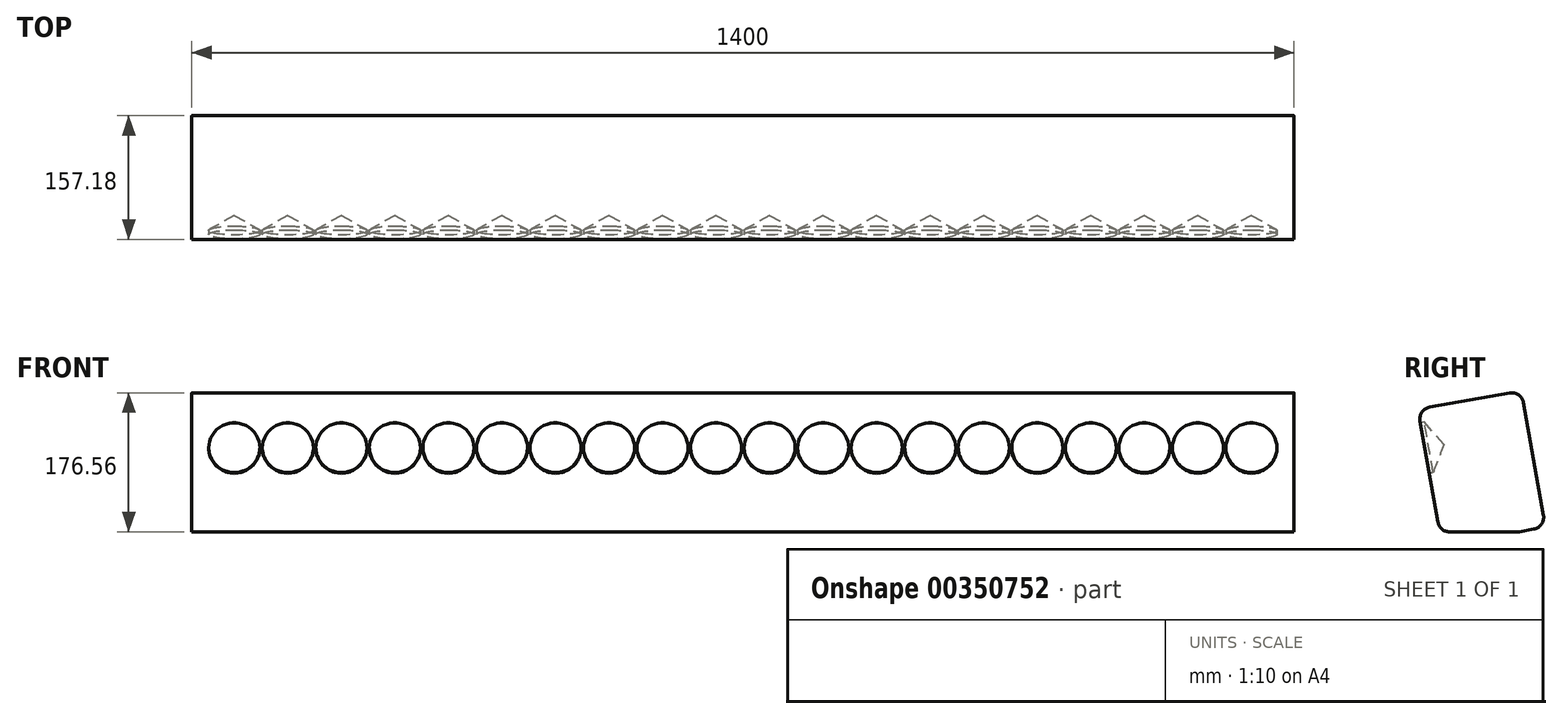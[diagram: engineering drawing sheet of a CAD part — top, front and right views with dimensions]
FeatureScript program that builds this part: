
annotation { "Feature Type Name" : "Feature", "Feature Type Description" : "" }
export const myFeature = defineFeature(function(context is Context, id is Id, definition is map)
    precondition{}
    {
        {
            var Q0;
            Q0=qCreatedBy(makeId("Right.planeOp"),FACE);
            var sketch = newSketch(context, id + "F0", { "sketchPlane" : qUnion([Q0])});
            skLineSegment(sketch, "E0", {"start": v(0, 0) * mm, "end": v(100, 0) * mm});
            skLineSegment(sketch, "E1", {"start": v(100, 0) * mm, "end": v(134.47, 6.08) * mm});
            skLineSegment(sketch, "E2", {"start": v(134.47, 6.08) * mm, "end": v(103.99, 178.94) * mm});
            skLineSegment(sketch, "E3", {"start": v(103.99, 178.94) * mm, "end": v(-27.46, 155.76) * mm});
            skLineSegment(sketch, "E4", {"start": v(-27.46, 155.76) * mm, "end": v(0, 0) * mm});
            skLineSegment(sketch, "E5", {"start": v(0, 0) * mm, "end": v(-507.71, 0) * mm, "construction": true});
            skLineSegment(sketch, "E6", {"start": v(-507.71, 0) * mm, "end": v(-15.3, 86.82) * mm, "construction": true});
            skSolve(sketch);
        }
        {
            var Q0;
            Q0=makeQuery(id+"F0.imprint","IMPRINT",FACE,{"disambiguationData":[TD([[makeQuery(id+"F0.imprint","IMPRINT",EDGE,{"derivedFrom":sQuery(id+"F0.wireOp",EDGE,"E0")}),1.0]])]});
            extrude(context, id + "F1", {"entities" : qUnion([Q0]), "endBound" : BoundingType.SYMMETRIC, "depth" : 1400 * mm});
        }
        {
            var Q0;
            Q0=makeQuery(id+"F1.opExtrude","SWEPT_EDGE",EDGE,{"disambiguationData":[OSD([sQuery(id+"F0.wireOp",EDGE,"E0"),sQuery(id+"F0.wireOp",EDGE,"E1")])]});
            var Q1;
            Q1=makeQuery(id+"F1.opExtrude","SWEPT_EDGE",EDGE,{"disambiguationData":[OSD([sQuery(id+"F0.wireOp",EDGE,"E1"),sQuery(id+"F0.wireOp",EDGE,"E2")])]});
            var Q2;
            Q2=makeQuery(id+"F1.opExtrude","SWEPT_EDGE",EDGE,{"disambiguationData":[OSD([sQuery(id+"F0.wireOp",EDGE,"E2"),sQuery(id+"F0.wireOp",EDGE,"E3")])]});
            var Q3;
            Q3=makeQuery(id+"F1.opExtrude","SWEPT_EDGE",EDGE,{"disambiguationData":[OSD([sQuery(id+"F0.wireOp",EDGE,"E3"),sQuery(id+"F0.wireOp",EDGE,"E4")])]});
            var Q4;
            Q4=makeQuery(id+"F1.opExtrude","SWEPT_EDGE",EDGE,{"disambiguationData":[OSD([sQuery(id+"F0.wireOp",EDGE,"E0"),sQuery(id+"F0.wireOp",EDGE,"E4")])]});
            fillet(context, id + "F2", {"entities" : qUnion([Q0, Q1, Q2, Q3, Q4]), "radius" : 15 * mm, "tangentPropagation" : true, "allowEdgeOverflow" : false});
        }
        {
            var Q0;
            Q0=makeQuery(id+"F1.opExtrude","SWEPT_FACE",FACE,{"disambiguationData":[OSD([sQuery(id+"F0.wireOp",EDGE,"E4")])]});
            var sketch = newSketch(context, id + "F3", { "sketchPlane" : qUnion([Q0])});
            skPoint(sketch, "E7", {"position": v(-34, 108.16) * mm});
            skPoint(sketch, "E8", {"position": v(34, 108.16) * mm});
            skLineSegment(sketch, "E9", {"start": v(-34, 108.16) * mm, "end": v(34, 108.16) * mm, "construction": true});
            skLineSegment(sketch, "E10", {"start": v(0, 0) * mm, "end": v(0, 108.16) * mm, "construction": true});
            skPoint(sketch, "E10.endSnap0", {"position": v(0, 12.59) * mm});
            skPoint(sketch, "E11.1.0.0", {"position": v(102, 108.16) * mm});
            skPoint(sketch, "E11.2.0.0", {"position": v(170, 108.16) * mm});
            skPoint(sketch, "E11.3.0.0", {"position": v(238, 108.16) * mm});
            skPoint(sketch, "E11.4.0.0", {"position": v(306, 108.16) * mm});
            skPoint(sketch, "E11.5.0.0", {"position": v(374, 108.16) * mm});
            skPoint(sketch, "E11.6.0.0", {"position": v(442, 108.16) * mm});
            skPoint(sketch, "E11.7.0.0", {"position": v(510, 108.16) * mm});
            skPoint(sketch, "E11.8.0.0", {"position": v(578, 108.16) * mm});
            skPoint(sketch, "E11.9.0.0", {"position": v(646, 108.16) * mm});
            skLineSegment(sketch, "E11.direction1", {"start": v(34, 108.16) * mm, "end": v(102, 108.16) * mm, "construction": true});
            skPoint(sketch, "E12.1.0.0", {"position": v(-102, 108.16) * mm});
            skPoint(sketch, "E12.2.0.0", {"position": v(-170, 108.16) * mm});
            skPoint(sketch, "E12.3.0.0", {"position": v(-238, 108.16) * mm});
            skPoint(sketch, "E12.4.0.0", {"position": v(-306, 108.16) * mm});
            skPoint(sketch, "E12.5.0.0", {"position": v(-374, 108.16) * mm});
            skPoint(sketch, "E12.6.0.0", {"position": v(-442, 108.16) * mm});
            skPoint(sketch, "E12.7.0.0", {"position": v(-510, 108.16) * mm});
            skPoint(sketch, "E12.8.0.0", {"position": v(-578, 108.16) * mm});
            skPoint(sketch, "E12.9.0.0", {"position": v(-646, 108.16) * mm});
            skLineSegment(sketch, "E12.direction1", {"start": v(-34, 108.16) * mm, "end": v(-102, 108.16) * mm, "construction": true});
            skSolve(sketch);
        }
        {
            var Q0;
            Q0=sQuery(id+"F3.wireOp",VERTEX,"E12.10.0.0");
            var Q1;
            Q1=sQuery(id+"F3.wireOp",VERTEX,"E12.9.0.0");
            var Q2;
            Q2=sQuery(id+"F3.wireOp",VERTEX,"E12.8.0.0");
            var Q3;
            Q3=sQuery(id+"F3.wireOp",VERTEX,"E12.7.0.0");
            var Q4;
            Q4=sQuery(id+"F3.wireOp",VERTEX,"E12.6.0.0");
            var Q5;
            Q5=sQuery(id+"F3.wireOp",VERTEX,"E12.5.0.0");
            var Q6;
            Q6=sQuery(id+"F3.wireOp",VERTEX,"E12.4.0.0");
            var Q7;
            Q7=sQuery(id+"F3.wireOp",VERTEX,"E12.3.0.0");
            var Q8;
            Q8=sQuery(id+"F3.wireOp",VERTEX,"E12.2.0.0");
            var Q9;
            Q9=sQuery(id+"F3.wireOp",VERTEX,"E12.1.0.0");
            var Q10;
            Q10=sQuery(id+"F3.wireOp",VERTEX,"E7");
            var Q11;
            Q11=sQuery(id+"F3.wireOp",VERTEX,"E8");
            var Q12;
            Q12=sQuery(id+"F3.wireOp",VERTEX,"E11.1.0.0");
            var Q13;
            Q13=sQuery(id+"F3.wireOp",VERTEX,"E11.2.0.0");
            var Q14;
            Q14=sQuery(id+"F3.wireOp",VERTEX,"E11.3.0.0");
            var Q15;
            Q15=sQuery(id+"F3.wireOp",VERTEX,"E11.4.0.0");
            var Q16;
            Q16=sQuery(id+"F3.wireOp",VERTEX,"E11.5.0.0");
            var Q17;
            Q17=sQuery(id+"F3.wireOp",VERTEX,"E11.6.0.0");
            var Q18;
            Q18=sQuery(id+"F3.wireOp",VERTEX,"E11.7.0.0");
            var Q19;
            Q19=sQuery(id+"F3.wireOp",VERTEX,"E11.8.0.0");
            var Q20;
            Q20=sQuery(id+"F3.wireOp",VERTEX,"E11.9.0.0");
            var Q21;
            Q21=sQuery(id+"F3.wireOp",VERTEX,"E11.10.0.0");
            var Q22;
            Q22=makeQuery(id+"F1.opExtrude","SWEPT_BODY",BODY,{"disambiguationData":[OSD([sQuery(id+"F0.wireOp",EDGE,"E0"),sQuery(id+"F0.wireOp",EDGE,"E1"),sQuery(id+"F0.wireOp",EDGE,"E2"),sQuery(id+"F0.wireOp",EDGE,"E3"),sQuery(id+"F0.wireOp",EDGE,"E4")])]});
            hole(context, id + "F4", {"style" : HoleStyle.SIMPLE, "endStyle" : HoleEndStyle.BLIND, "holeDiameter" : 65 * mm, "holeDepth" : 5 * mm, "isTappedThrough" : true, "tappedDepth" : 12 * mm, "tapClearance" : 3, "locations" : qUnion([Q0, Q1, Q2, Q3, Q4, Q5, Q6, Q7, Q8, Q9, Q10, Q11, Q12, Q13, Q14, Q15, Q16, Q17, Q18, Q19, Q20, Q21]), "scope" : qUnion([Q22])});
        }
    });
